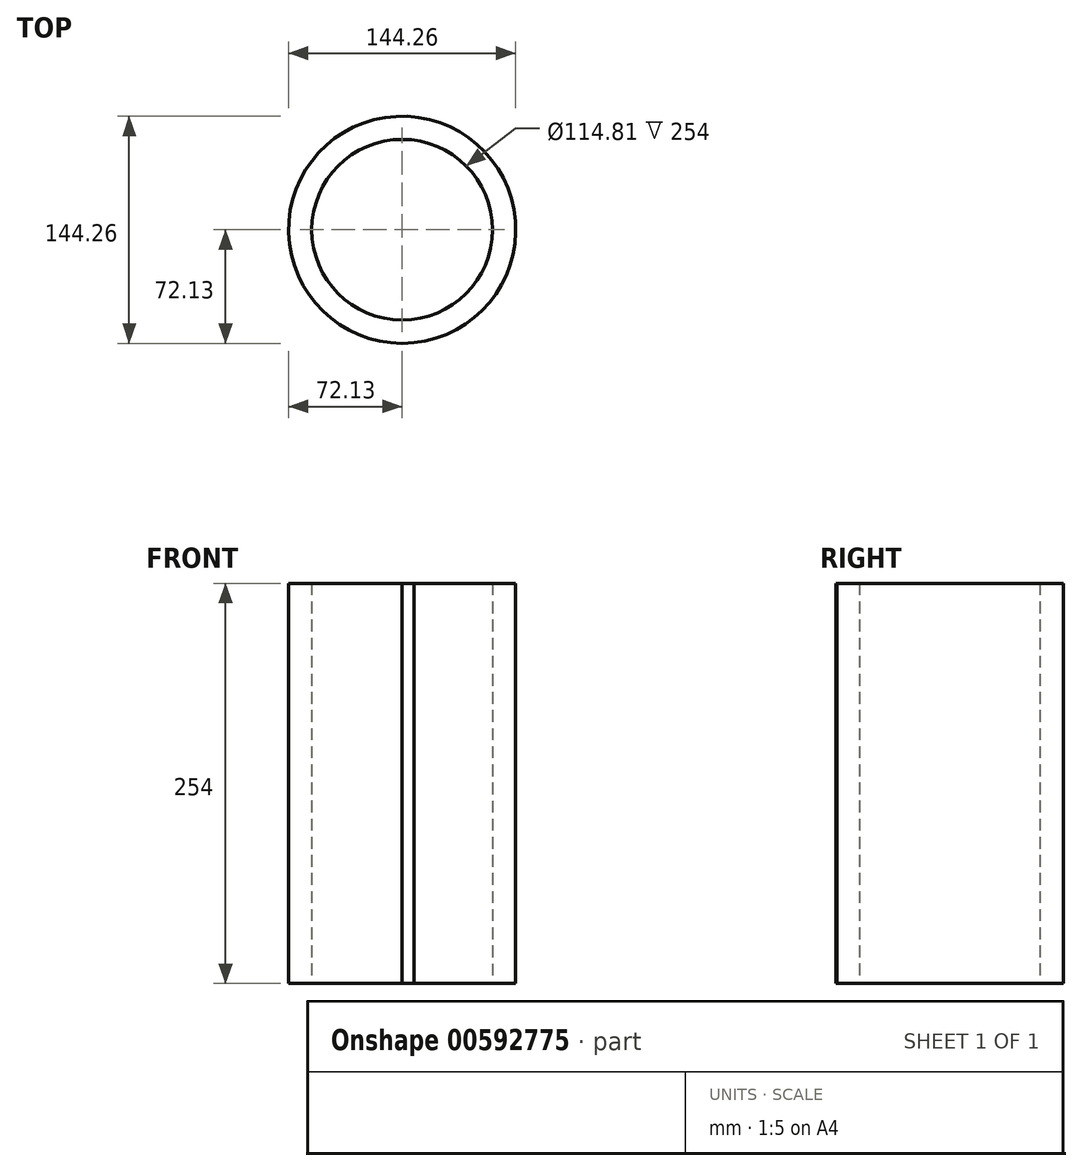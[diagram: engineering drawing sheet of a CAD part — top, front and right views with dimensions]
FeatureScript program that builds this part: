
annotation { "Feature Type Name" : "Feature", "Feature Type Description" : "" }
export const myFeature = defineFeature(function(context is Context, id is Id, definition is map)
    precondition{}
    {
        {
            var Q0;
            Q0=qCreatedBy(makeId("Top.planeOp"),FACE);
            var sketch = newSketch(context, id + "F0", { "sketchPlane" : qUnion([Q0])});
            skCircle(sketch, "E0", {"center": v(0, 0) * mm, "radius": 72.13 * mm});
            skCircle(sketch, "E1", {"center": v(0, 0) * mm, "radius": 57.4 * mm});
            skCircle(sketch, "E2", {"center": v(172.13, 0) * mm, "radius": 63.08 * mm});
            skCircle(sketch, "E3", {"center": v(172.13, 0) * mm, "radius": 50.52 * mm});
            skLineSegment(sketch, "E4", {"start": v(0, -72.13) * mm, "end": v(175.42, -63) * mm});
            skLineSegment(sketch, "E5", {"start": v(175.42, -63) * mm, "end": v(168.85, 63) * mm});
            skLineSegment(sketch, "E6", {"start": v(168.85, 63) * mm, "end": v(0, 72.24) * mm});
            skSolve(sketch);
        }
        {
            var Q0;
            Q0=makeQuery(id+"F0.imprint","IMPRINT",FACE,{"disambiguationData":[TD([[makeQuery(id+"F0.imprint","IMPRINT",EDGE,{"derivedFrom":sQuery(id+"F0.wireOp",EDGE,"E1")}),-1.0]])]});
            var Q1;
            Q1=sQuery(id+"F0.wireOp",EDGE,"E4");
            extrude(context, id + "F1", {"entities" : qUnion([Q0]), "surfaceEntities" : qUnion([Q1]), "depth" : 254 * mm, "offsetDistance" : 25.4 * mm});
        }
        {
            var Q0;
            Q0=makeQuery(id+"F1.opExtrude","CAP_FACE",FACE,{"disambiguationData":[OSD([sQuery(id+"F0.wireOp",EDGE,"E0"),sQuery(id+"F0.wireOp",EDGE,"E1"),sQuery(id+"F0.wireOp",EDGE,"E4")])],"isStart":false});
            extrude(context, id + "F2", {"entities" : qUnion([Q0]), "operationType" : NewBodyOperationType.ADD, "oppositeDirection" : true, "depth" : 50.8 * mm, "offsetDistance" : 25.4 * mm});
        }
    });
